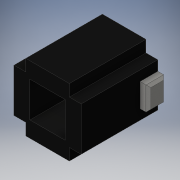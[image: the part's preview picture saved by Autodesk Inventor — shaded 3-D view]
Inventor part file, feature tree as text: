
AUTODESK INVENTOR PART (.ipt)
format: ipt  version: 2016 (Build 200138000, 138)  size: 134,144 bytes
history: native  units: in
note: dims shown in document units (in); Inventor stores cm internally (conversion verified against a paired STEP export)
features: extrude x2, sketch x2, chamfer x1
ambient origin geometry x8: Origin, YZ Plane, XZ Plane, XY Plane, X Axis, Y Axis, Z Axis, Center Point
bodies: Solid1 (feature_tree)
feature tree (5):
  extrude  "Extrusion1"  Depth=1.122in
  extrude  "Extrusion2"  Depth=2.2441in
  chamfer  "Chamfer1"  Distance=1.1811in
  sketch  "Sketch1"  dims[d0=1.122in d1=1.122in]
  sketch  "Sketch2"  dims[d2=2.2441in d3=2.2441in d4=1.1811in d5=1.1811in d6=0.5906in d7=0.5906in d8=0.3937in d9=0.3937in d10=0.3937in d11=0.3937in d12=0.3937in d13=0.3937in d14=0.3937in d15=2.5591in d16=0.0in d17=0.3937in d20=0.5906in d22=0.7874in d23=0.2756in d24=0.0in d25=0.0787in d26=0.0787in d27=45.0deg]
